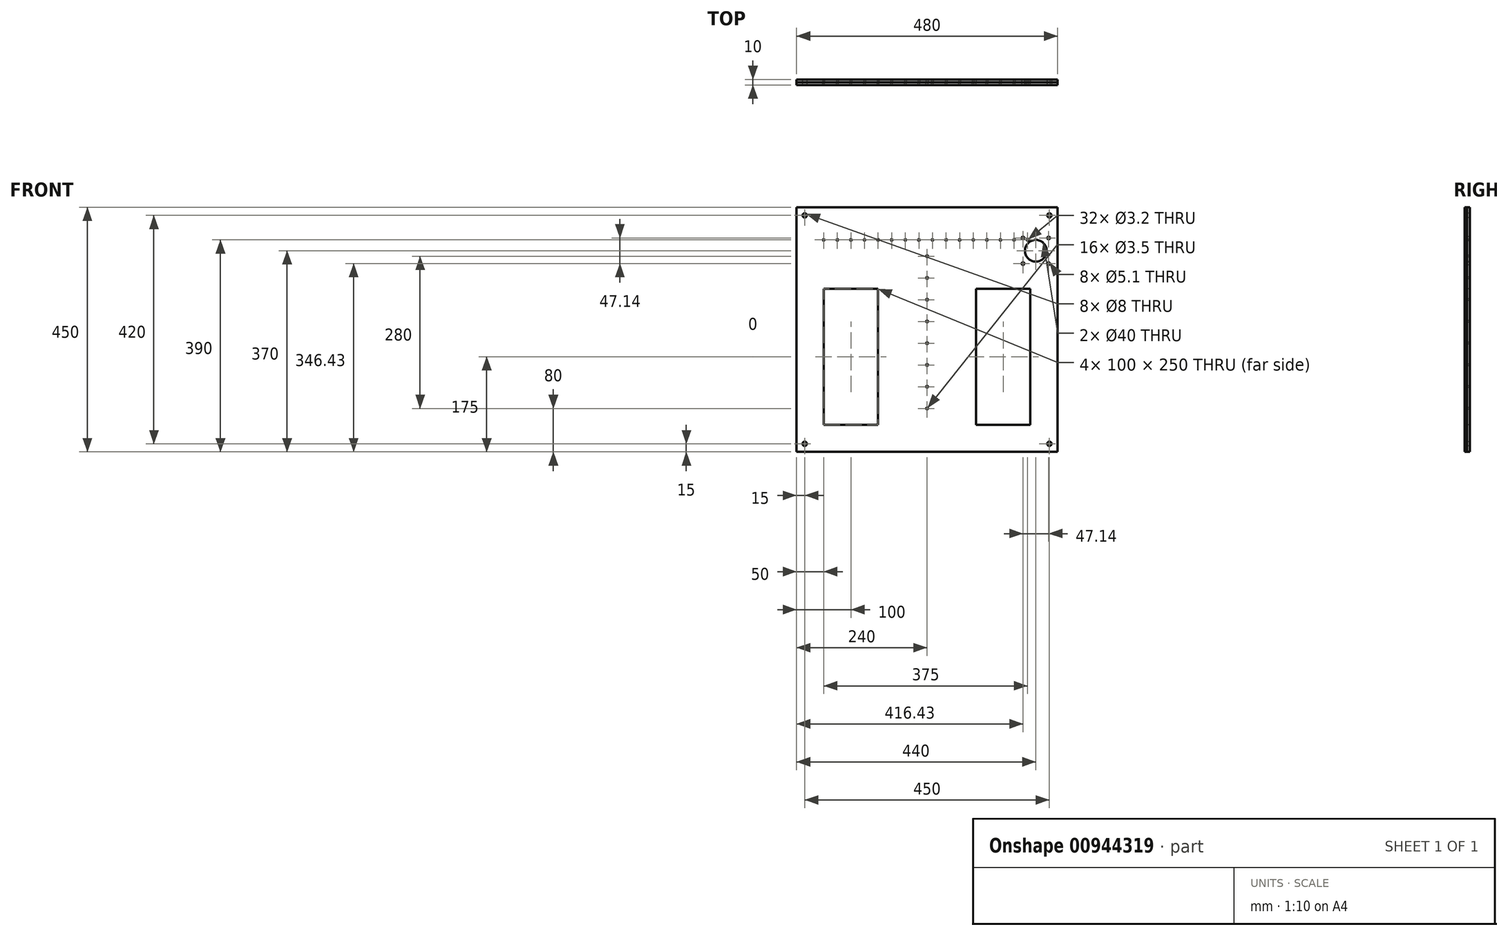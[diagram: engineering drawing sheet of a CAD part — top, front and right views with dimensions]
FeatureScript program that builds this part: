
annotation { "Feature Type Name" : "Feature", "Feature Type Description" : "" }
export const myFeature = defineFeature(function(context is Context, id is Id, definition is map)
    precondition{}
    {
        {
            var Q0;
            Q0=qCreatedBy(makeId("Front.planeOp"),FACE);
            var sketch = newSketch(context, id + "F0", { "sketchPlane" : qUnion([Q0])});
            skLineSegment(sketch, "E0.bottom", {"start": v(0, 0) * mm, "end": v(480, 0) * mm});
            skLineSegment(sketch, "E0.top", {"start": v(0, 450) * mm, "end": v(480, 450) * mm});
            skLineSegment(sketch, "E0.left", {"start": v(0, 0) * mm, "end": v(0, 450) * mm});
            skLineSegment(sketch, "E0.right", {"start": v(480, 0) * mm, "end": v(480, 450) * mm});
            skLineSegment(sketch, "E1", {"start": v(240, 0) * mm, "end": v(240, 450) * mm, "construction": true});
            skLineSegment(sketch, "E2", {"start": v(20.39, 390) * mm, "end": v(471, 390) * mm, "construction": true});
            skCircle(sketch, "E3", {"center": v(50, 390) * mm, "radius": 1.6 * mm});
            skCircle(sketch, "E4.1.0.0", {"center": v(75, 390) * mm, "radius": 1.6 * mm});
            skCircle(sketch, "E4.2.0.0", {"center": v(100, 390) * mm, "radius": 1.6 * mm});
            skCircle(sketch, "E4.3.0.0", {"center": v(125, 390) * mm, "radius": 1.6 * mm});
            skCircle(sketch, "E4.4.0.0", {"center": v(150, 390) * mm, "radius": 1.6 * mm});
            skCircle(sketch, "E4.5.0.0", {"center": v(175, 390) * mm, "radius": 1.6 * mm});
            skCircle(sketch, "E4.6.0.0", {"center": v(200, 390) * mm, "radius": 1.6 * mm});
            skCircle(sketch, "E4.7.0.0", {"center": v(225, 390) * mm, "radius": 1.6 * mm});
            skCircle(sketch, "E4.8.0.0", {"center": v(250, 390) * mm, "radius": 1.6 * mm});
            skLineSegment(sketch, "E4.direction1", {"start": v(50, 390) * mm, "end": v(75, 390) * mm, "construction": true});
            skLineSegment(sketch, "E5.bottom", {"start": v(50, 50) * mm, "end": v(150, 50) * mm});
            skLineSegment(sketch, "E5.top", {"start": v(50, 300) * mm, "end": v(150, 300) * mm});
            skLineSegment(sketch, "E5.left", {"start": v(50, 50) * mm, "end": v(50, 300) * mm});
            skLineSegment(sketch, "E5.right", {"start": v(150, 50) * mm, "end": v(150, 300) * mm});
            skLineSegment(sketch, "E6.MirrorCS", {"start": v(430, 300) * mm, "end": v(330, 300) * mm});
            skLineSegment(sketch, "E7.MirrorCS", {"start": v(330, 50) * mm, "end": v(330, 300) * mm});
            skLineSegment(sketch, "E8.MirrorCS", {"start": v(430, 50) * mm, "end": v(330, 50) * mm});
            skLineSegment(sketch, "E9.MirrorCS", {"start": v(430, 50) * mm, "end": v(430, 300) * mm});
            skLineSegment(sketch, "E10", {"start": v(240, -186.91) * mm, "end": v(240, 485.92) * mm, "construction": true});
            skCircle(sketch, "E11", {"center": v(240, 80) * mm, "radius": 1.75 * mm});
            skCircle(sketch, "E12.1.0.0", {"center": v(240, 120) * mm, "radius": 1.75 * mm});
            skCircle(sketch, "E12.2.0.0", {"center": v(240, 160) * mm, "radius": 1.75 * mm});
            skCircle(sketch, "E12.3.0.0", {"center": v(240, 200) * mm, "radius": 1.75 * mm});
            skCircle(sketch, "E12.4.0.0", {"center": v(240, 240) * mm, "radius": 1.75 * mm});
            skCircle(sketch, "E12.5.0.0", {"center": v(240, 280) * mm, "radius": 1.75 * mm});
            skCircle(sketch, "E12.6.0.0", {"center": v(240, 320) * mm, "radius": 1.75 * mm});
            skCircle(sketch, "E12.7.0.0", {"center": v(240, 360) * mm, "radius": 1.75 * mm});
            skLineSegment(sketch, "E12.direction1", {"start": v(240, 80) * mm, "end": v(240, 120) * mm, "construction": true});
            skCircle(sketch, "E13.0.9.0", {"center": v(275, 390) * mm, "radius": 1.6 * mm});
            skCircle(sketch, "E13.0.10.0", {"center": v(300, 390) * mm, "radius": 1.6 * mm});
            skCircle(sketch, "E13.0.11.0", {"center": v(325, 390) * mm, "radius": 1.6 * mm});
            skCircle(sketch, "E13.0.12.0", {"center": v(350, 390) * mm, "radius": 1.6 * mm});
            skCircle(sketch, "E13.0.13.0", {"center": v(375, 390) * mm, "radius": 1.6 * mm});
            skCircle(sketch, "E13.0.14.0", {"center": v(400, 390) * mm, "radius": 1.6 * mm});
            skCircle(sketch, "E13.0.15.0", {"center": v(425, 390) * mm, "radius": 1.6 * mm});
            skSolve(sketch);
        }
        {
            var Q0;
            Q0=makeQuery(id+"F0.imprint","IMPRINT",FACE,{"disambiguationData":[TD([[makeQuery(id+"F0.imprint","IMPRINT",EDGE,{"derivedFrom":sQuery(id+"F0.wireOp",EDGE,"E0.bottom")}),1.0]])]});
            extrude(context, id + "F1", {"entities" : qUnion([Q0]), "depth" : 5 * mm, "offsetDistance" : 25 * mm});
        }
        {
            var Q0;
            Q0 = qSketchRegion(id + "F0", true);
            extrude(context, id + "F2", {"entities" : qUnion([Q0]), "oppositeDirection" : true, "depth" : 5 * mm, "offsetDistance" : 25 * mm});
        }
        {
            var Q0;
            Q0=makeQuery(id+"F1.opExtrude","CAP_FACE",FACE,{"disambiguationData":[OSD([sQuery(id+"F0.wireOp",EDGE,"E0.bottom"),sQuery(id+"F0.wireOp",EDGE,"E0.top"),sQuery(id+"F0.wireOp",EDGE,"E0.left"),sQuery(id+"F0.wireOp",EDGE,"E0.right"),sQuery(id+"F0.wireOp",EDGE,"E3"),sQuery(id+"F0.wireOp",EDGE,"E4.1.0.0"),sQuery(id+"F0.wireOp",EDGE,"E4.2.0.0"),sQuery(id+"F0.wireOp",EDGE,"E4.3.0.0"),sQuery(id+"F0.wireOp",EDGE,"E4.4.0.0"),sQuery(id+"F0.wireOp",EDGE,"E4.5.0.0"),sQuery(id+"F0.wireOp",EDGE,"E4.6.0.0"),sQuery(id+"F0.wireOp",EDGE,"E4.7.0.0"),sQuery(id+"F0.wireOp",EDGE,"E4.8.0.0"),sQuery(id+"F0.wireOp",EDGE,"E5.bottom"),sQuery(id+"F0.wireOp",EDGE,"E5.top"),sQuery(id+"F0.wireOp",EDGE,"E5.left"),sQuery(id+"F0.wireOp",EDGE,"E5.right"),sQuery(id+"F0.wireOp",EDGE,"E6.MirrorCS"),sQuery(id+"F0.wireOp",EDGE,"E7.MirrorCS"),sQuery(id+"F0.wireOp",EDGE,"E8.MirrorCS"),sQuery(id+"F0.wireOp",EDGE,"E9.MirrorCS"),sQuery(id+"F0.wireOp",EDGE,"E11"),sQuery(id+"F0.wireOp",EDGE,"E12.1.0.0"),sQuery(id+"F0.wireOp",EDGE,"E12.2.0.0"),sQuery(id+"F0.wireOp",EDGE,"E12.3.0.0"),sQuery(id+"F0.wireOp",EDGE,"E12.4.0.0"),sQuery(id+"F0.wireOp",EDGE,"E12.5.0.0"),sQuery(id+"F0.wireOp",EDGE,"E12.6.0.0"),sQuery(id+"F0.wireOp",EDGE,"E12.7.0.0"),sQuery(id+"F0.wireOp",EDGE,"bcd95837-61dc-42b3-8797-2649a7e9edce0.MirrorC"),sQuery(id+"F0.wireOp",EDGE,"0607b469-407f-4239-9ca9-e0c1080f221b0.MirrorC"),sQuery(id+"F0.wireOp",EDGE,"E13.0.9.0"),sQuery(id+"F0.wireOp",EDGE,"E13.0.10.0"),sQuery(id+"F0.wireOp",EDGE,"E13.0.11.0"),sQuery(id+"F0.wireOp",EDGE,"E13.0.12.0"),sQuery(id+"F0.wireOp",EDGE,"E13.0.13.0"),sQuery(id+"F0.wireOp",EDGE,"E13.0.14.0"),sQuery(id+"F0.wireOp",EDGE,"E13.0.15.0"),sQuery(id+"F0.wireOp",EDGE,"ZQUOVBqP-Bax5-jSvb-jhna-KkN9Fs2Kzp6w"),sQuery(id+"F0.wireOp",EDGE,"bc146e59-67b8-434f-a245-5dca26289ae70.MirrorC"),sQuery(id+"F0.wireOp",EDGE,"0c65702c-dda1-4483-baa8-2285ec15aa3c0.MirrorC"),sQuery(id+"F0.wireOp",EDGE,"471a4cb1-79a8-4583-9a81-3d21a7b9fa300.MirrorC"),sQuery(id+"F0.wireOp",EDGE,"Snh46oHW-7TZJ-rpDi-rR6a-EmG7XmuDHJg8")])],"isStart":false});
            var sketch = newSketch(context, id + "F3", { "sketchPlane" : qUnion([Q0])});
            skLineSegment(sketch, "E14", {"start": v(440, 411.81) * mm, "end": v(440, 305.24) * mm, "construction": true});
            skLineSegment(sketch, "E15", {"start": v(26.03, 370) * mm, "end": v(533.12, 370) * mm, "construction": true});
            skCircle(sketch, "E16", {"center": v(463.57, 346.43) * mm, "radius": 2.55 * mm});
            skCircle(sketch, "E17.MirrorC", {"center": v(416.43, 346.43) * mm, "radius": 2.55 * mm});
            skCircle(sketch, "E18.MirrorC", {"center": v(463.57, 393.57) * mm, "radius": 2.55 * mm});
            skCircle(sketch, "E19.MirrorC", {"center": v(416.43, 393.57) * mm, "radius": 2.55 * mm});
            skCircle(sketch, "E20", {"center": v(440, 370) * mm, "radius": 20 * mm});
            skCircle(sketch, "E21", {"center": v(15, 435) * mm, "radius": 4 * mm});
            skCircle(sketch, "E22", {"center": v(465, 435) * mm, "radius": 4 * mm});
            skCircle(sketch, "E23", {"center": v(465, 15) * mm, "radius": 4 * mm});
            skCircle(sketch, "E24", {"center": v(15, 15) * mm, "radius": 4 * mm});
            skSolve(sketch);
        }
        {
            var Q0;
            Q0 = qSketchRegion(id + "F3", true);
            extrude(context, id + "F4", {"entities" : qUnion([Q0]), "operationType" : NewBodyOperationType.REMOVE, "endBound" : BoundingType.THROUGH_ALL, "oppositeDirection" : true, "depth" : 25 * mm, "offsetDistance" : 25 * mm});
        }
    });
